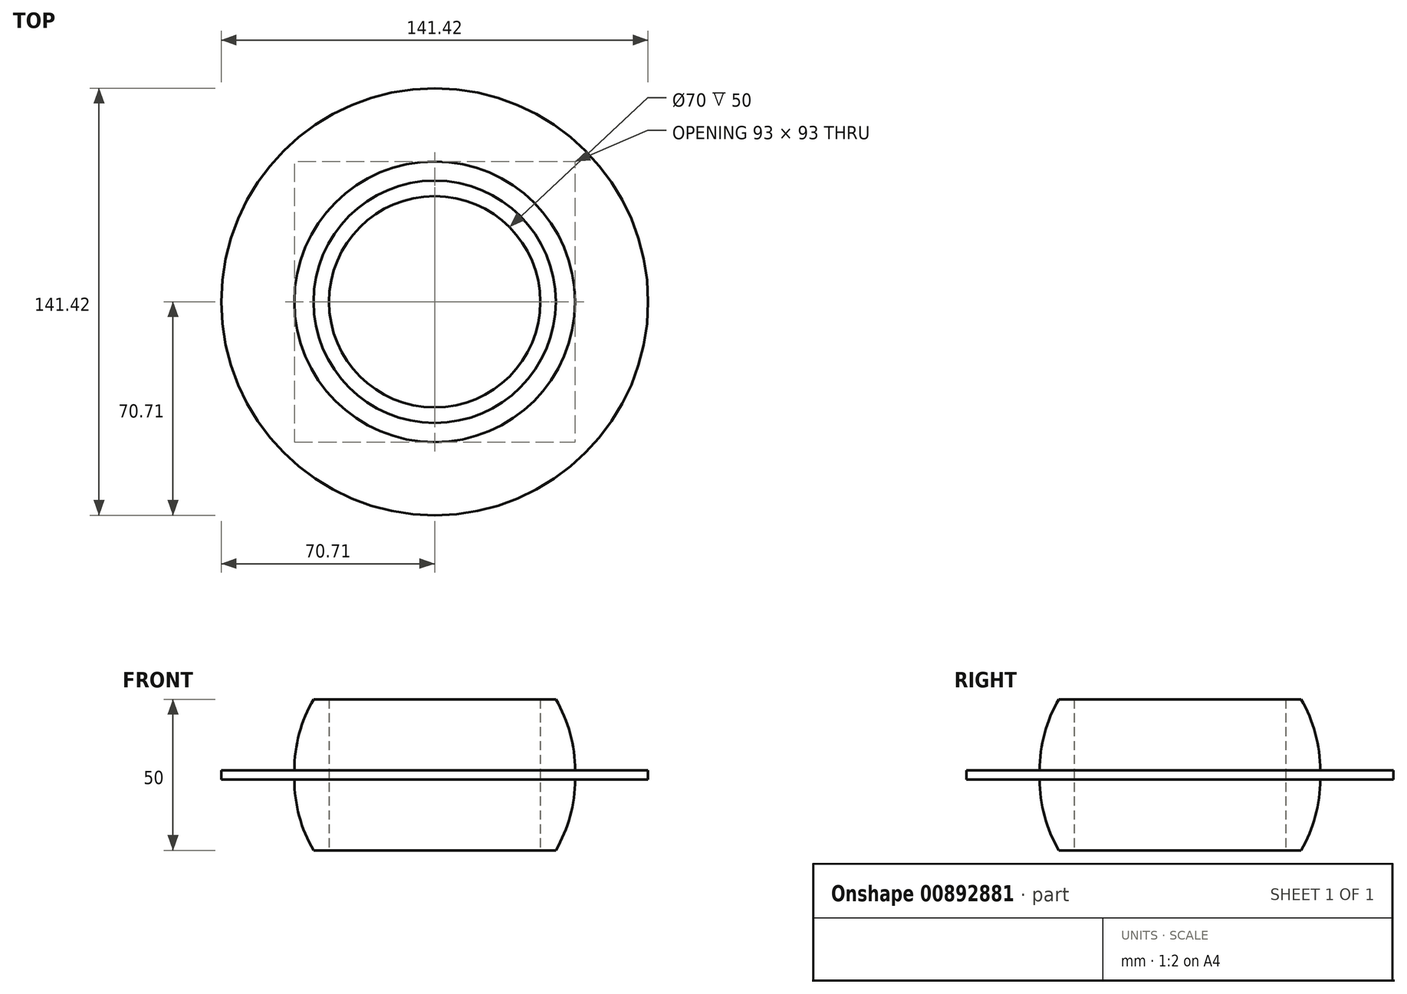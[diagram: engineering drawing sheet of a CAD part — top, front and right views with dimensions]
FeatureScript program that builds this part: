
annotation { "Feature Type Name" : "Feature", "Feature Type Description" : "" }
export const myFeature = defineFeature(function(context is Context, id is Id, definition is map)
    precondition{}
    {
        {
            assignVariable(context, id + "F0", {"name" : "dielectricWidthMM", "anyValue" : 3});
        }
        {
            var Q0;
            Q0=qCreatedBy(makeId("Top.planeOp"),FACE);
            var sketch = newSketch(context, id + "F1", { "sketchPlane" : qUnion([Q0])});
            skCircle(sketch, "E0", {"center": v(0, 0) * mm, "radius": 46.5 * mm});
            skLineSegment(sketch, "E1", {"start": v(-46.5, 0) * mm, "end": v(46.5, 0) * mm});
            skCircle(sketch, "E2", {"center": v(0, 0) * mm, "radius": 70.71 * mm});
            skSolve(sketch);
        }
        {
            var Q0;
            {var subQ0=sQuery(id+"F1.wireOp",EDGE,"E1");Q0=makeQuery(id+"F1.imprint","IMPRINT",FACE,{"disambiguationData":[TD([[makeQuery(id+"F1.imprint","IMPRINT",EDGE,{"derivedFrom":subQ0}),-1.0]])]});}
            var Q1;
            Q1=sQuery(id+"F1.wireOp",EDGE,"E1");
            revolve(context, id + "F2", {"surfaceOperationType" : NewSurfaceOperationType.NEW, "entities" : qUnion([Q0]), "axis" : qUnion([Q1]), "revolveType" : RevolveType.ONE_DIRECTION, "angle" : 180 * degree});
        }
        {
            var Q0;
            Q0=makeQuery(id+"F1.imprint","IMPRINT",FACE,{"disambiguationData":[TD([[makeQuery(id+"F1.imprint","IMPRINT",EDGE,{"derivedFrom":sQuery(id+"F1.wireOp",EDGE,"E2")}),1.0]])]});
            var Q1;
            {var subQ0=sQuery(id+"F1.wireOp",EDGE,"E1");Q1=makeQuery(id+"F1.imprint","IMPRINT",FACE,{"disambiguationData":[TD([[makeQuery(id+"F1.imprint","IMPRINT",EDGE,{"derivedFrom":subQ0}),1.0]])]});}
            var Q2;
            {var subQ0=sQuery(id+"F1.wireOp",EDGE,"E1");Q2=makeQuery(id+"F1.imprint","IMPRINT",FACE,{"disambiguationData":[TD([[makeQuery(id+"F1.imprint","IMPRINT",EDGE,{"derivedFrom":subQ0}),-1.0]])]});}
            extrude(context, id + "F3", {"entities" : qUnion([Q0, Q1, Q2]), "operationType" : NewBodyOperationType.ADD, "depth" : (getVariable(context, 'dielectricWidthMM')) * mm, "offsetDistance" : 25 * mm});
        }
        {
            var Q0;
            Q0=makeQuery(id+"F3.opExtrude","CAP_FACE",FACE,{"disambiguationData":[OSD([sQuery(id+"F1.wireOp",EDGE,"E2")])],"isStart":false});
            var sketch = newSketch(context, id + "F4", { "sketchPlane" : qUnion([Q0])});
            skLineSegment(sketch, "E3.0", {"start": v(-46.5, 0) * mm, "end": v(46.5, 0) * mm});
            skCircle(sketch, "E4.0", {"center": v(0, 0) * mm, "radius": 46.5 * mm});
            skSolve(sketch);
        }
        {
            var Q0;
            {var subQ0=sQuery(id+"F4.wireOp",EDGE,"E3.0");Q0=makeQuery(id+"F4.imprint","IMPRINT",FACE,{"disambiguationData":[TD([[makeQuery(id+"F4.imprint","IMPRINT",EDGE,{"derivedFrom":subQ0}),-1.0]])]});}
            var Q1;
            Q1=sQuery(id+"F4.wireOp",EDGE,"E3.0");
            revolve(context, id + "F5", {"operationType" : NewBodyOperationType.ADD, "surfaceOperationType" : NewSurfaceOperationType.NEW, "entities" : qUnion([Q0]), "axis" : qUnion([Q1]), "revolveType" : RevolveType.ONE_DIRECTION, "oppositeDirection" : true, "angle" : 180 * degree});
        }
        {
            var Q0;
            Q0=qCreatedBy(makeId("Front.planeOp"),FACE);
            var sketch = newSketch(context, id + "F6", { "sketchPlane" : qUnion([Q0])});
            skLineSegment(sketch, "E5", {"start": v(0, 0) * mm, "end": v(0, -23.5) * mm, "construction": true});
            skLineSegment(sketch, "E6", {"start": v(0, 0) * mm, "end": v(0, 26.5) * mm, "construction": true});
            skSolve(sketch);
        }
        {
            var Q0;
            Q0=sQuery(id+"F6.wireOp",VERTEX,"E6.end");
            var Q1;
            Q1=qCreatedBy(makeId("Top.planeOp"),FACE);
            cPlane(context, id + "F7", {"entities" : qUnion([Q0, Q1]), "cplaneType" : CPlaneType.PLANE_POINT, "offset" : 25 * mm, "width" : 150 * mm, "height" : 150 * mm});
        }
        {
            var Q0;
            Q0=qCreatedBy(id+"F7.planeOp",FACE);
            var sketch = newSketch(context, id + "F8", { "sketchPlane" : qUnion([Q0])});
            skLineSegment(sketch, "E7.bottom", {"start": v(50, 50) * mm, "end": v(-50, 50) * mm});
            skLineSegment(sketch, "E7.top", {"start": v(50, -50) * mm, "end": v(-50, -50) * mm});
            skLineSegment(sketch, "E7.left", {"start": v(50, 50) * mm, "end": v(50, -50) * mm});
            skLineSegment(sketch, "E7.right", {"start": v(-50, 50) * mm, "end": v(-50, -50) * mm});
            skPoint(sketch, "E7.middle", {"position": v(0, 0) * mm});
            skSolve(sketch);
        }
        {
            var Q0;
            Q0 = qSketchRegion(id + "F8", true);
            extrude(context, id + "F9", {"entities" : qUnion([Q0]), "operationType" : NewBodyOperationType.REMOVE, "depth" : 25 * mm, "offsetDistance" : 25 * mm});
        }
        {
            var Q0;
            Q0=sQuery(id+"F6.wireOp",VERTEX,"E5.end");
            var Q1;
            Q1=qCreatedBy(makeId("Top.planeOp"),FACE);
            cPlane(context, id + "F10", {"entities" : qUnion([Q0, Q1]), "cplaneType" : CPlaneType.PLANE_POINT, "offset" : 25 * mm, "width" : 150 * mm, "height" : 150 * mm});
        }
        {
            var Q0;
            Q0=qCreatedBy(id+"F10.planeOp",FACE);
            var sketch = newSketch(context, id + "F11", { "sketchPlane" : qUnion([Q0])});
            skLineSegment(sketch, "E8.bottom", {"start": v(50, 50) * mm, "end": v(-50, 50) * mm});
            skLineSegment(sketch, "E8.top", {"start": v(50, -50) * mm, "end": v(-50, -50) * mm});
            skLineSegment(sketch, "E8.left", {"start": v(50, 50) * mm, "end": v(50, -50) * mm});
            skLineSegment(sketch, "E8.right", {"start": v(-50, 50) * mm, "end": v(-50, -50) * mm});
            skPoint(sketch, "E8.middle", {"position": v(0, 0) * mm});
            skSolve(sketch);
        }
        {
            var Q0;
            Q0 = qSketchRegion(id + "F11", true);
            extrude(context, id + "F12", {"entities" : qUnion([Q0]), "operationType" : NewBodyOperationType.REMOVE, "oppositeDirection" : true, "depth" : 25 * mm, "offsetDistance" : 25 * mm});
        }
        {
            var Q0;
            Q0=qCreatedBy(makeId("Top.planeOp"),FACE);
            var sketch = newSketch(context, id + "F13", { "sketchPlane" : qUnion([Q0])});
            skCircle(sketch, "E9", {"center": v(0, 0) * mm, "radius": 35 * mm});
            skSolve(sketch);
        }
        {
            var Q0;
            Q0 = qSketchRegion(id + "F13", true);
            extrude(context, id + "F14", {"entities" : qUnion([Q0]), "operationType" : NewBodyOperationType.REMOVE, "endBound" : BoundingType.THROUGH_ALL, "depth" : 50 * mm, "offsetDistance" : 25 * mm, "hasSecondDirection" : true, "secondDirectionBound" : SecondDirectionBoundingType.THROUGH_ALL, "secondDirectionOppositeDirection" : true, "secondDirectionDepth" : 25 * mm});
        }
    });
